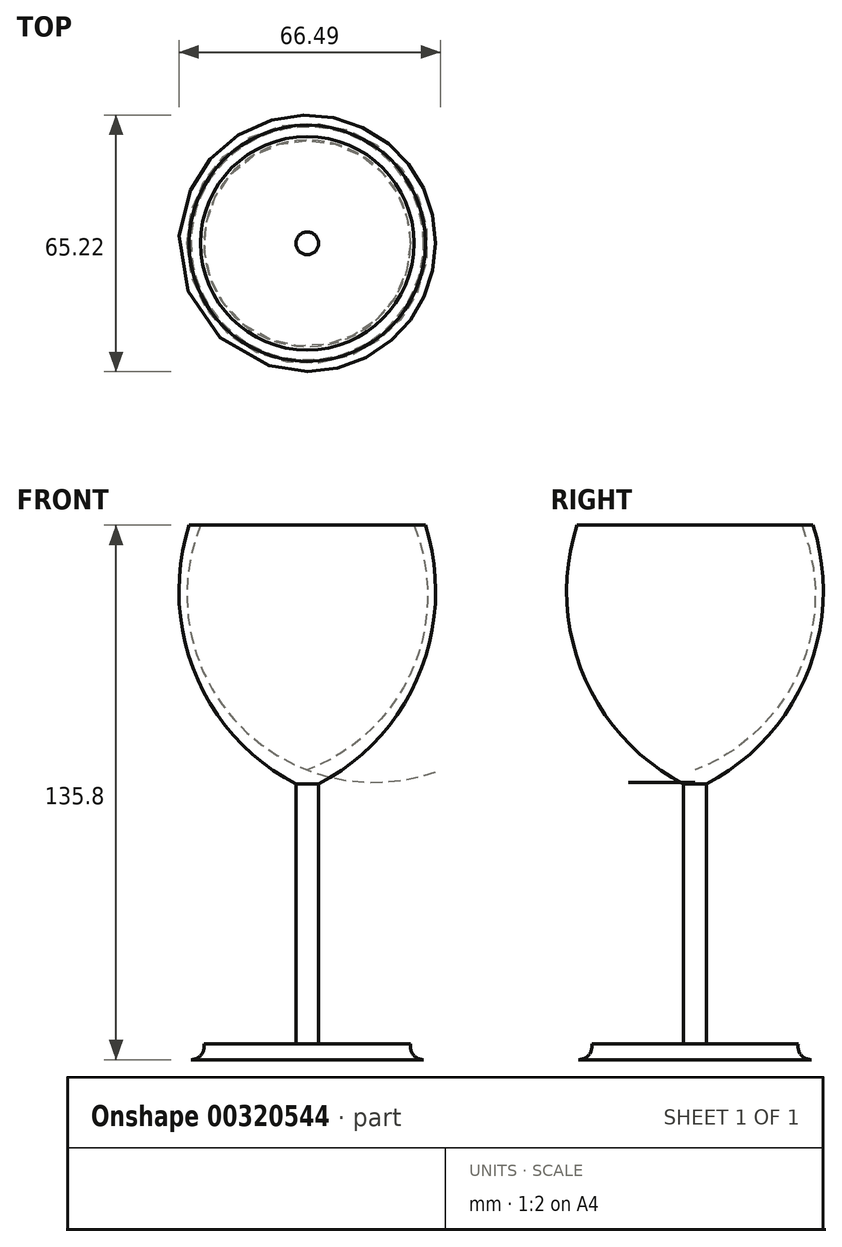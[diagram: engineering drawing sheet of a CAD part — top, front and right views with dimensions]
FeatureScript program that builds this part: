
annotation { "Feature Type Name" : "Feature", "Feature Type Description" : "" }
export const myFeature = defineFeature(function(context is Context, id is Id, definition is map)
    precondition{}
    {
        {
            var Q0;
            Q0=qCreatedBy(makeId("Front.planeOp"),FACE);
            var sketch = newSketch(context, id + "F0", { "sketchPlane" : qUnion([Q0])});
            skLineSegment(sketch, "E0", {"start": v(0, -62.9) * mm, "end": v(-29.56, -62.9) * mm});
            skArc(sketch, "E1", {"start": v(-29.56, -62.9) * mm, "mid": v(-26.96, -61.68) * mm, "end": v(-26.23, -58.9) * mm});
            skLineSegment(sketch, "E2", {"start": v(-26.23, -58.9) * mm, "end": v(-2.89, -58.9) * mm});
            skLineSegment(sketch, "E3", {"start": v(-2.89, -58.9) * mm, "end": v(-2.89, 7.11) * mm});
            skArc(sketch, "E4", {"start": v(-30, 72.9) * mm, "mid": v(-28.44, 35.06) * mm, "end": v(-2.89, 7.11) * mm});
            skLineSegment(sketch, "E5", {"start": v(-30, 72.9) * mm, "end": v(-27.11, 72.9) * mm});
            skArc(sketch, "E6", {"start": v(-27.11, 72.9) * mm, "mid": v(-26.63, 36.09) * mm, "end": v(0, 10.67) * mm});
            skLineSegment(sketch, "E7", {"start": v(0, 10.67) * mm, "end": v(0, -62.9) * mm});
            skSolve(sketch);
        }
        {
            var Q0;
            Q0=makeQuery(id+"F0.imprint","IMPRINT",FACE,{"disambiguationData":[TD([[makeQuery(id+"F0.imprint","IMPRINT",EDGE,{"derivedFrom":sQuery(id+"F0.wireOp",EDGE,"E0")}),-1.0]])]});
            var Q1;
            Q1=sQuery(id+"F0.wireOp",EDGE,"E7");
            revolve(context, id + "F1", {"entities" : qUnion([Q0]), "axis" : qUnion([Q1]), "revolveType" : RevolveType.FULL});
        }
    });
